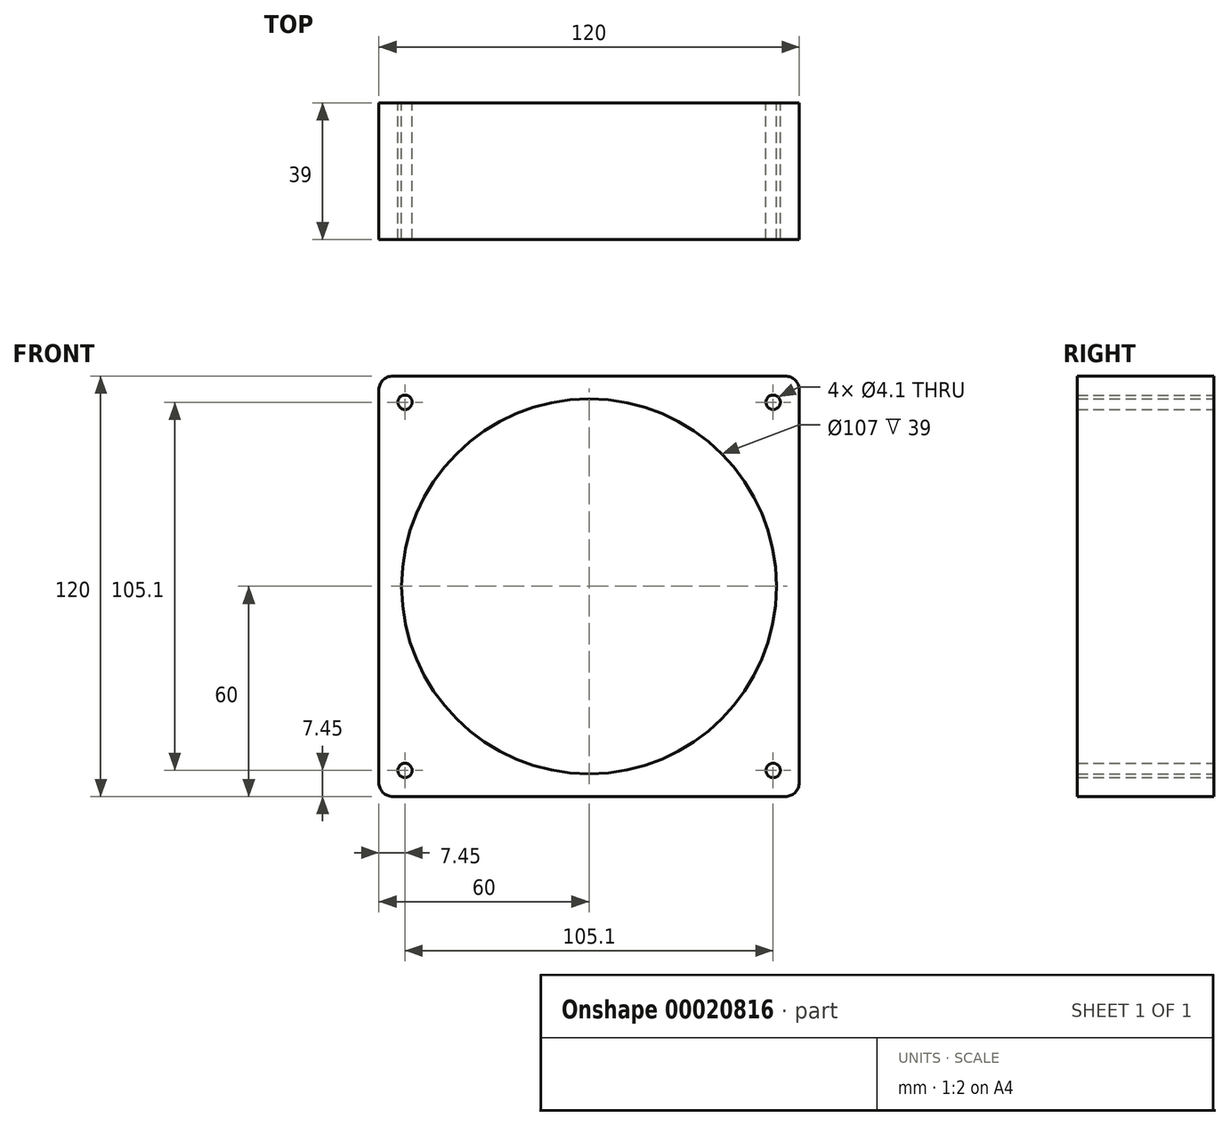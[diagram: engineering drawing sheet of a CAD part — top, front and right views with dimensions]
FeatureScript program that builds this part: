
annotation { "Feature Type Name" : "Feature", "Feature Type Description" : "" }
export const myFeature = defineFeature(function(context is Context, id is Id, definition is map)
    precondition{}
    {
        {
            var Q0;
            Q0=qCreatedBy(makeId("Front.planeOp"),FACE);
            var sketch = newSketch(context, id + "F0", { "sketchPlane" : qUnion([Q0])});
            skLineSegment(sketch, "E0.rect.bottom", {"start": v(0, 60) * mm, "end": v(-56, 60) * mm});
            skLineSegment(sketch, "E0.rect.right", {"start": v(-60, 56) * mm, "end": v(-60, 0) * mm});
            skPoint(sketch, "E0.rect.middle", {"position": v(0, 0) * mm});
            skPoint(sketch, "E1.visualSharp", {"position": v(-60, 60) * mm});
            skArc(sketch, "E1.filletArc", {"start": v(-56, 60) * mm, "mid": v(-58.83, 58.83) * mm, "end": v(-60, 56) * mm});
            skCircle(sketch, "E2", {"center": v(-52.55, 52.55) * mm, "radius": 2.05 * mm});
            skLineSegment(sketch, "E3", {"start": v(0, 64.82) * mm, "end": v(0, -64.53) * mm, "construction": true});
            skLineSegment(sketch, "E4", {"start": v(64.04, 0) * mm, "end": v(-64.61, 0) * mm, "construction": true});
            skLineSegment(sketch, "E5.MirrorCS", {"start": v(0, 60) * mm, "end": v(56, 60) * mm});
            skArc(sketch, "E6.MirrorCS", {"start": v(56, 60) * mm, "mid": v(58.83, 58.83) * mm, "end": v(60, 56) * mm});
            skCircle(sketch, "E7.MirrorC", {"center": v(52.55, 52.55) * mm, "radius": 2.05 * mm});
            skLineSegment(sketch, "E8.MirrorCS", {"start": v(60, 56) * mm, "end": v(60, 0) * mm});
            skLineSegment(sketch, "E9.MirrorCS", {"start": v(-60, -56) * mm, "end": v(-60, 0) * mm});
            skArc(sketch, "E10.MirrorCS", {"start": v(-56, -60) * mm, "mid": v(-58.83, -58.83) * mm, "end": v(-60, -56) * mm});
            skLineSegment(sketch, "E11.MirrorCS", {"start": v(0, -60) * mm, "end": v(-56, -60) * mm});
            skCircle(sketch, "E12.MirrorC", {"center": v(-52.55, -52.55) * mm, "radius": 2.05 * mm});
            skLineSegment(sketch, "E13.MirrorCS", {"start": v(0, -60) * mm, "end": v(56, -60) * mm});
            skArc(sketch, "E14.MirrorCS", {"start": v(56, -60) * mm, "mid": v(58.83, -58.83) * mm, "end": v(60, -56) * mm});
            skLineSegment(sketch, "E15.MirrorCS", {"start": v(60, -56) * mm, "end": v(60, 0) * mm});
            skCircle(sketch, "E16.MirrorC", {"center": v(52.55, -52.55) * mm, "radius": 2.05 * mm});
            skCircle(sketch, "E17", {"center": v(0, 0) * mm, "radius": 53.5 * mm});
            skSolve(sketch);
        }
        {
            var Q0;
            Q0=makeQuery(id+"F0.imprint","IMPRINT",FACE,{"disambiguationData":[TD([[makeQuery(id+"F0.imprint","IMPRINT",EDGE,{"derivedFrom":sQuery(id+"F0.wireOp",EDGE,"E0.rect.bottom")}),1.0]])]});
            extrude(context, id + "F1", {"entities" : qUnion([Q0]), "depth" : 39 * mm});
        }
    });
